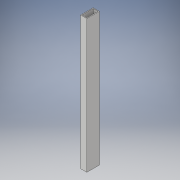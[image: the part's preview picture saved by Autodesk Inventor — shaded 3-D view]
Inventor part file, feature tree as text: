
AUTODESK INVENTOR PART (.ipt)
format: ipt  version: 2018 (Build 220112000, 112)  size: 101,376 bytes
history: native  units: in
note: dims shown in document units (in); Inventor stores cm internally (conversion verified against a paired STEP export)
features: extrude x1, sketch x1
ambient origin geometry x8: Origin, YZ Plane, XZ Plane, XY Plane, X Axis, Y Axis, Z Axis, Center Point
bodies: Solid1 (feature_tree)
feature tree (2):
  extrude  "Extrusion1"  Depth=2.0in
  sketch  "Sketch1"  dims[d0=1.0in d1=2.0in d2=0.125in d3=0.125in d4=0.125in d5=0.125in d6=21.0in d7=0.0in]
